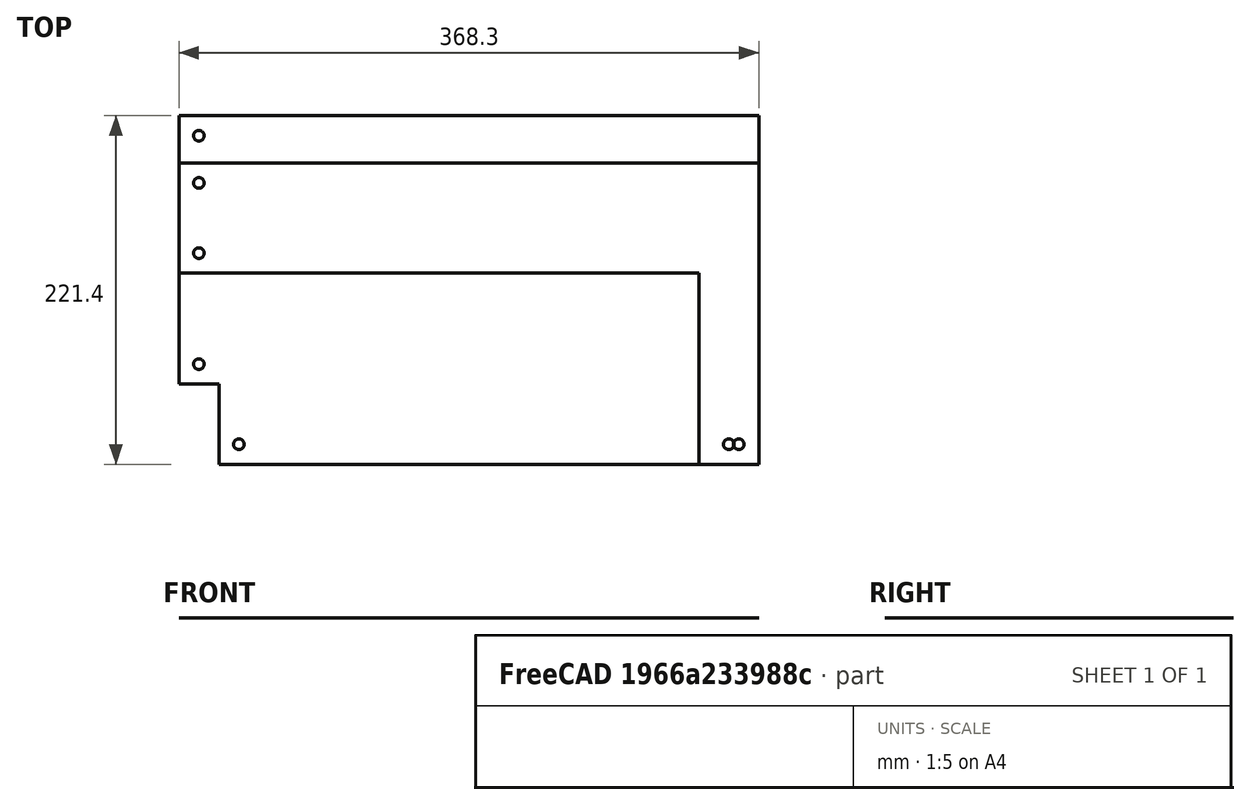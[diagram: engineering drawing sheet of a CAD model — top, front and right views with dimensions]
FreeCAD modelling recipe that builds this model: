
FCSTD DOCUMENT  (FreeCAD 0.18.4R)
Label: darkbox_baffle
License: All rights reserved
LicenseURL: http://en.wikipedia.org/wiki/All_rights_reserved
objects: Part::Part2DObjectPython×7, Part::Cut×5, Part::FeaturePython×3, Spreadsheet::Sheet×1
note: 15 computed .brp shape members not serialized (recipe doc carries the construction recipe); baked Part::Feature solids carry a one-line shape summary decoded from their .brp

FEATURE [Spreadsheet::Sheet] Spreadsheet  label="params"
  cells = A1=Name; B1=Value; C1=Notes; A2=cable_space_length; B2(cable_space_length)==12in; A3=cable_space_outside_height; B3(cable_space_outside_height)==96mm; C3=max(brush_passthru_height, outside_corner_bracket_heigh) (= brush height); A4=baffle_overlap_height; B4(baffle_overlap_height)==7cm; A5=inside_wall_extra_length; B5(inside_wall_extra_length)==1.5in; A6=outside_wall_hook_length; B6(outside_wall_hook_length)==1.5in; A8=rail_width; B8(rail_width)==1in; A9=mounting_hole_diam; B9(mounting_hole_diam)==0.266in; A10=extra_outside_wall_height; B10(extra_outside_wall_height)==3cm; A11=inside_corner_bracket_height; B11(inside_corner_bracket_height)==25.5mm
FEATURE [Part::Part2DObjectPython] Rectangle  label="outer_wall_rect1"  # Draft 2D object (typed FeaturePython)
  ChamferSize = 0
  FilletRadius = 0
  Height = 100
  Length = 330.2
  MakeFace = true
  MapMode = 5
  Placement = pos=(0,121.4,0) rot=(0,0,1;0rad)
  expr: Placement.Base.y = params.cable_space_outside_height + params.rail_width
  expr: Length = params.cable_space_length + params.rail_width
  expr: Height = params.baffle_overlap_height + params.extra_outside_wall_height
FEATURE [Part::Part2DObjectPython] Rectangle001  label="outer_wall_hook"  # Draft 2D object (typed FeaturePython)
  ChamferSize = 0
  Columns = 1
  FilletRadius = 0
  Height = 221.4
  Length = 38.1
  MakeFace = true
  Placement = pos=(330.2,0,0) rot=(0,0,1;0rad)
  Rows = 1
  expr: Length = params.outside_wall_hook_length
  expr: Placement.Base.y = 0
  expr: Height = outer_wall_rect1.Height + params.cable_space_outside_height + params.rail_width
  expr: Placement.Base.x = outer_wall_rect1.Placement.Base.x + outer_wall_rect1.Length
FEATURE [Part::Part2DObjectPython] Circle  label="mounting_hole"  # Draft 2D object (typed FeaturePython)
  FirstAngle = 0
  LastAngle = 0
  MakeFace = true
  Radius = 3.3782
  expr: Radius = params.mounting_hole_diam / 2
FEATURE [Part::Part2DObjectPython] Fusion  label="outer_wall_noholes"  # Draft 2D object (typed FeaturePython)
  Base = -> Rectangle
  ChamferSize = 0
  Closed = true
  End = (330.2,121.4,0)
  FilletRadius = 0
  Length = 0
  MakeFace = true
  Points = (7) [(330.2,0,0),(368.3,0,0),(368.3,221.4,0),(330.2,221.4,0),(0,221.4,0),(0,121.4,0),(330.2,121.4,0)]
  Start = (330.2,0,0)
  Subdivisions = 0
  Tool = -> Rectangle001
FEATURE [Part::FeaturePython] Array  label="outer_vertical_mounting_holes"  # Draft array (typed FeaturePython)
  Angle = 360
  ArrayType = 0
  Axis = (0,0,1)
  Base = -> Circle
  Center = (0,0,0)
  Fuse = false
  IntervalAxis = (0,0,0)
  IntervalX = (1,0,0)
  IntervalY = (0,74.6,0)
  IntervalZ = (0,0,1)
  NumberPolar = 1
  NumberX = 1
  NumberY = 2
  NumberZ = 1
  Placement = pos=(12.7,134.1,0) rot=(0,0,1;0rad)
  expr: IntervalY.y = outer_wall_rect1.Height - params.rail_width
  expr: Placement.Base.x = params.rail_width / 2
  expr: Placement.Base.y = outer_wall_rect1.Placement.Base.y + params.rail_width / 2
FEATURE [Part::Part2DObjectPython] Clone2D  label="outer_bottom_mounting_hole"  # Draft 2D object (typed FeaturePython)
  Fuse = false
  Objects = -> [Circle]
  Placement = pos=(349.25,12.7,0) rot=(0,0,1;0rad)
  Scale = (1,1,1)
  expr: Placement.Base.y = params.rail_width / 2
  expr: Placement.Base.x = outer_wall_hook.Placement.Base.x + outer_wall_hook.Length / 2
FEATURE [Part::Cut] Cut  label="outer_wall_vertical_holes"
  Base = -> Fusion
  Tool = -> Array
FEATURE [Part::Cut] Cut001  label="outer_wall_nofillet"
  Base = -> Cut
  Tool = -> Clone2D
FEATURE [Part::Part2DObjectPython] Rectangle002  label="inner_wall_rect"  # Draft 2D object (typed FeaturePython)
  ChamferSize = 0
  Columns = 1
  FilletRadius = 0
  Height = 191.4
  Length = 368.3
  MakeFace = true
  Rows = 1
  expr: Length = outer_wall_rect1.Length + params.inside_wall_extra_length
  expr: Height = outer_wall_rect1.Placement.Base.y + params.baffle_overlap_height
FEATURE [Part::Part2DObjectPython] Rectangle003  label="inner_wall_to_subtract"  # Draft 2D object (typed FeaturePython)
  ChamferSize = 0
  Columns = 1
  FilletRadius = 0
  Height = 50.9
  Length = 25.4
  MakeFace = true
  Rows = 1
  expr: Height = params.rail_width + params.inside_corner_bracket_height
  expr: Length = params.rail_width
FEATURE [Part::Cut] Cut002  label="inner_wall_noholes"
  Base = -> Rectangle002
  Tool = -> Rectangle003
FEATURE [Part::FeaturePython] Array001  label="inner_wall_vertical_holes"  # Draft array (typed FeaturePython)
  Angle = 360
  ArrayType = 0
  Axis = (0,0,1)
  Base = -> Circle
  Center = (0,0,0)
  Fuse = false
  IntervalAxis = (0,0,0)
  IntervalX = (1,0,0)
  IntervalY = (0,115.1,0)
  IntervalZ = (0,0,1)
  NumberPolar = 1
  NumberX = 1
  NumberY = 2
  NumberZ = 1
  Placement = pos=(12.7,63.6,0) rot=(0,0,1;0rad)
  expr: IntervalY.y = inner_wall_rect.Height - inner_wall_to_subtract.Height - params.rail_width
  expr: Placement.Base.y = inner_wall_to_subtract.Height + params.rail_width / 2
  expr: Placement.Base.x = params.rail_width / 2
FEATURE [Part::FeaturePython] Array002  label="inner_wall_horizontal_holes"  # Draft array (typed FeaturePython)
  Angle = 360
  ArrayType = 0
  Axis = (0,0,1)
  Base = -> Circle
  Center = (0,0,0)
  Fuse = false
  IntervalAxis = (0,0,0)
  IntervalX = (317.5,0,0)
  IntervalY = (0,1,0)
  IntervalZ = (0,0,1)
  NumberPolar = 1
  NumberX = 2
  NumberY = 1
  NumberZ = 1
  Placement = pos=(38.1,12.7,0) rot=(0,0,1;0rad)
  expr: IntervalX.x = inner_wall_rect.Length - inner_wall_to_subtract.Length - params.rail_width
  expr: Placement.Base.x = inner_wall_to_subtract.Length + params.rail_width / 2
  expr: Placement.Base.y = params.rail_width / 2
FEATURE [Part::Cut] Cut003  label="inner_wall_with_vert_holes"
  Base = -> Cut002
  Tool = -> Array001
FEATURE [Part::Cut] Cut004  label="inner_wall_nofillet"
  Base = -> Cut003
  Tool = -> Array002
